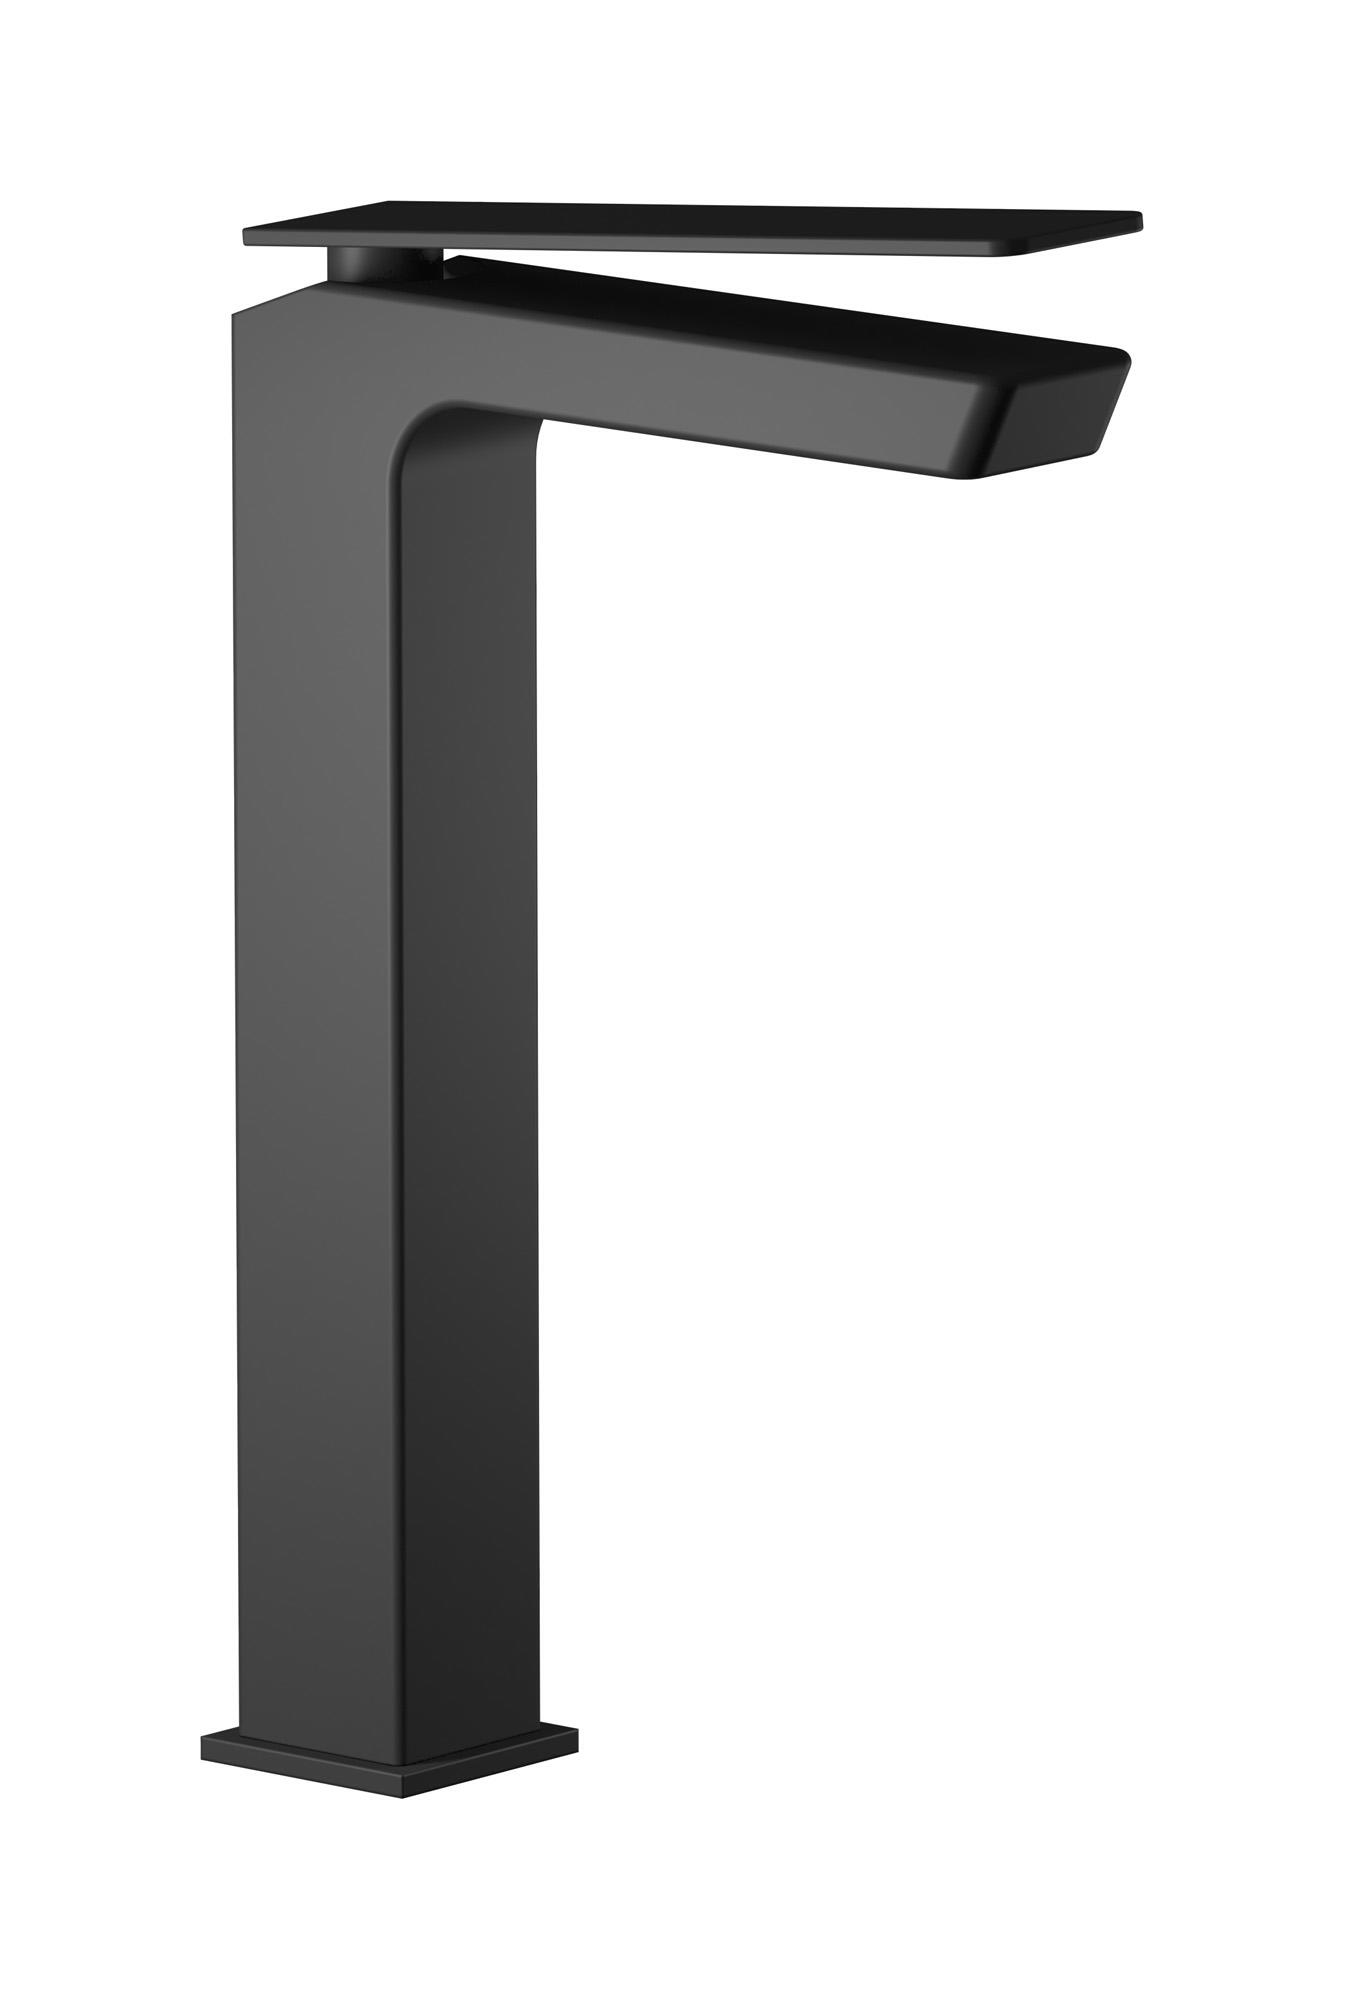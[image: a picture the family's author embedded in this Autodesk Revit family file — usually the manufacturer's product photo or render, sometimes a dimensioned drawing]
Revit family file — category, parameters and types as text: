
# Revit family: K3202
name_source: partatom
category: Apparecchi idraulici
units: mm (PartAtom-declared; Revit-internal decimal feet)

## family parameters
Basato su piano di lavoro = No
Condiviso = No
Mantieni orientamento annotazione = No
Numero OmniClass = 23.45.55.17
Punto di calcolo locali = No
Quota connettore circolare = Usa diametro
Sempre verticale = Sì
Taglio con vuoti quando caricato = No
Tipo di parte = Normale
Titolo OmniClass = Mixing Faucets

## types (8) — shared parameters
Cold water inlet = 10 mm  [stored 0.0328084 ft]
Commenti sul tipo = Washbasin mixer
Connessione CW = No
Connessione HW = No
Connessione di scarico = No
Connessione di ventilazione = No
Descrizione = Tall monohole washbasin mixer complete with drain
Hot water inlet = 10 mm  [stored 0.0328084 ft]
Produttore = IB Rubinetterie S.p.A.
URL = https://www.weareib.it
zero-valued in all types: Prospetto di default

## per-type parameters (varying)
| type | Finishes surface | Immagine tipo | Modello |
| Chrome | IB_Chrome | K3202CC.jpg | K3202CC |
| Brushed nickel | IB_Brushed nickel | K3202SS.jpg | K3202SS |
| Matt white | IB_matt white | K3202BO.jpg | K3202BO |
| Matt black | IB_matt black | K3202NP.jpg | K3202NP |
| Pale gold | IB_Pale gold | K3202II.jpg | K3202II |
| Brushed pale gold | IB_brushed pale gold | K3202IS.jpg | K3202IS |
| Rose gold | IB_Rose gold | K3202RS.jpg | K3202RS |
| Gold | IB_gold | K3202OO.jpg | K3202OO |

note: [stored X ft] marks values corroborated as IEEE doubles in the binary element streams (Revit-internal decimal feet)
